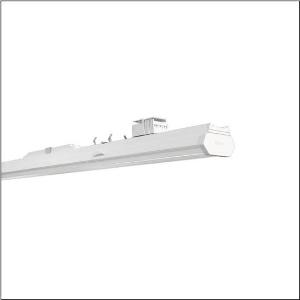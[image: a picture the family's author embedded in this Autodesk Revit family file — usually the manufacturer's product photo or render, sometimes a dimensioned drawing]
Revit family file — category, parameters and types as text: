
# Revit family: licross_r__11_protected_extreme_ho_51tp12dn4fxme_36ff
name_source: partatom
category: Lighting Fixtures
units: mm (PartAtom-declared; Revit-internal decimal feet)

## family parameters
Cut with Voids When Loaded = No
Host = Face
Light Source = No
Part Type = Normal
Room Calculation Point = No
Round Connector Dimension = Use Diameter
Shared = No

## types (1)
- --- (1 x LED, 15270 lm, 87.3 W, 4000K)
    Apparent Load = 87 VA
    CIE Flux Codes = 70 91 97 98 100
    Color Rendering = 80
    Color Temperature = 4000K
    Default Elevation = 1800 mm
    Description = Licross® 11 Protected extreme HO, luminaire insert, of sheet steel, galvanised, coil coated, white, length: 1.500mm, width: 90mm, height: 101mm, LED rated luminous flux: 15.270lm, light colour: 840, control gear: DALI 2, with plug, 5-pole, with phase selection, mains connection: 220..240V, AC, 50/60Hz, rated input power: 87W, halogen-free wiring, primary optical cover: cover, of PMMA, light emission: direct distribution, primary light characteristic: symmetric, protection rating (complete): IP64, insulation class (complete): insulation class I (protective earthing), certification: CE, ENEC, VDE, UKCA, protection symbol: D if used in an environment with conductive dust loads with corresponding accessories, impact resistance: IK06, permissible ambient temperature for indoor applications: -40..+40°C, corresponds to IFS (International Featured Standards) requirements for safety and quality in the food industry, reducing of maximum allowable ambient temperature of 5°C with ceiling mounting, LABS conformity tested according to VDMA 24364:2018-05, packaging unit: 1 piece
    Height = 92 mm
    Lamp = 1 x LED
    Lamp Light Flux = 15270 lm
    Lamp Power = 87.3 W
    Lamp count = 1
    Length = 1500 mm
    Luminous efficacy = 175 lm/W
    Manufacturer = Siteco
    ModVariant = No
    Model = 51TP12DN4FXME
    Mounting Place = Ceiling
    Mounting Type = Pendant
    Number of Poles = 1
    OnlyDefault = Yes
    Power Factor = 1
    Product Name = Licross® 11 Protected extreme HO
    Product group = luminaire insert
    ProductGroupID = 901
    Protection Class = Protection class I
    Protection Degree = IP 64
    RLX_Detail_Level = 1
    RLX_Emergency_Light_Flux = 0 lm
    RLX_Emergency_Type = 0
    RLX_Emergency_Type_DB = No
    RlxData = <blob elided: 24453 chars, md5=8779bfd6>
    Socket = socket
    Standby Power = 0 W
    System Light Flux = 15270 lm
    System Power = 87 W
    Type Comments = factory setting: luminous flux: 100 % | dim-lin: 254 | 589 mA
    Type Image = l_1256148.jpg
    URL = http://relux.com
    VarID = @adj_016373
    Voltage = 0 V
    Weight = 0.00 kg
    Width = 88 mm

## geometry (parser evidence)
native form markers: Blend x4, Sweep x9
no freeform markers — native parametric forms only
